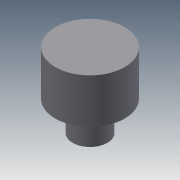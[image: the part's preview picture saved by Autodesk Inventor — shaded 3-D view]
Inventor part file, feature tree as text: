
AUTODESK INVENTOR PART (.ipt)
format: ipt  version: 2015 (Build 190159000, 159)  size: 89,600 bytes
history: native  units: mm
features: sketch x3, extrude x2, plane x1, hole x1
ambient origin geometry x8: Origin, YZ Plane, XZ Plane, XY Plane, X Axis, Y Axis, Z Axis, Center Point
bodies: Solid1 (feature_tree)
feature tree (7):
  extrude  "Extrusion1"  Depth=9.0mm TaperAngle=0.0deg
  plane  "Work Plane1"
  hole  "Hole1"  [1 undecoded]
  extrude  "Extrusion3"  Depth=6.0mm TaperAngle=0.0deg
  sketch  "Sketch1"  dims[d0=14.0mm d1=9.0mm d2=0.0mm]
  sketch  "Sketch3"  dims[d9=2.4mm]
  sketch  "Sketch4"  dims[d10=2.459mm d11=7.0mm d12=4.0mm d13=2.0mm d14=90.0deg d15=7.0mm d16=0.0mm d17=7.0mm d18=6.0mm d19=0.0mm]
note: 1 required parameter value undecoded (feature->parameter linkage not recoverable at this tier; creation-order binding heuristic only, values carry confidence <= 0.55)
